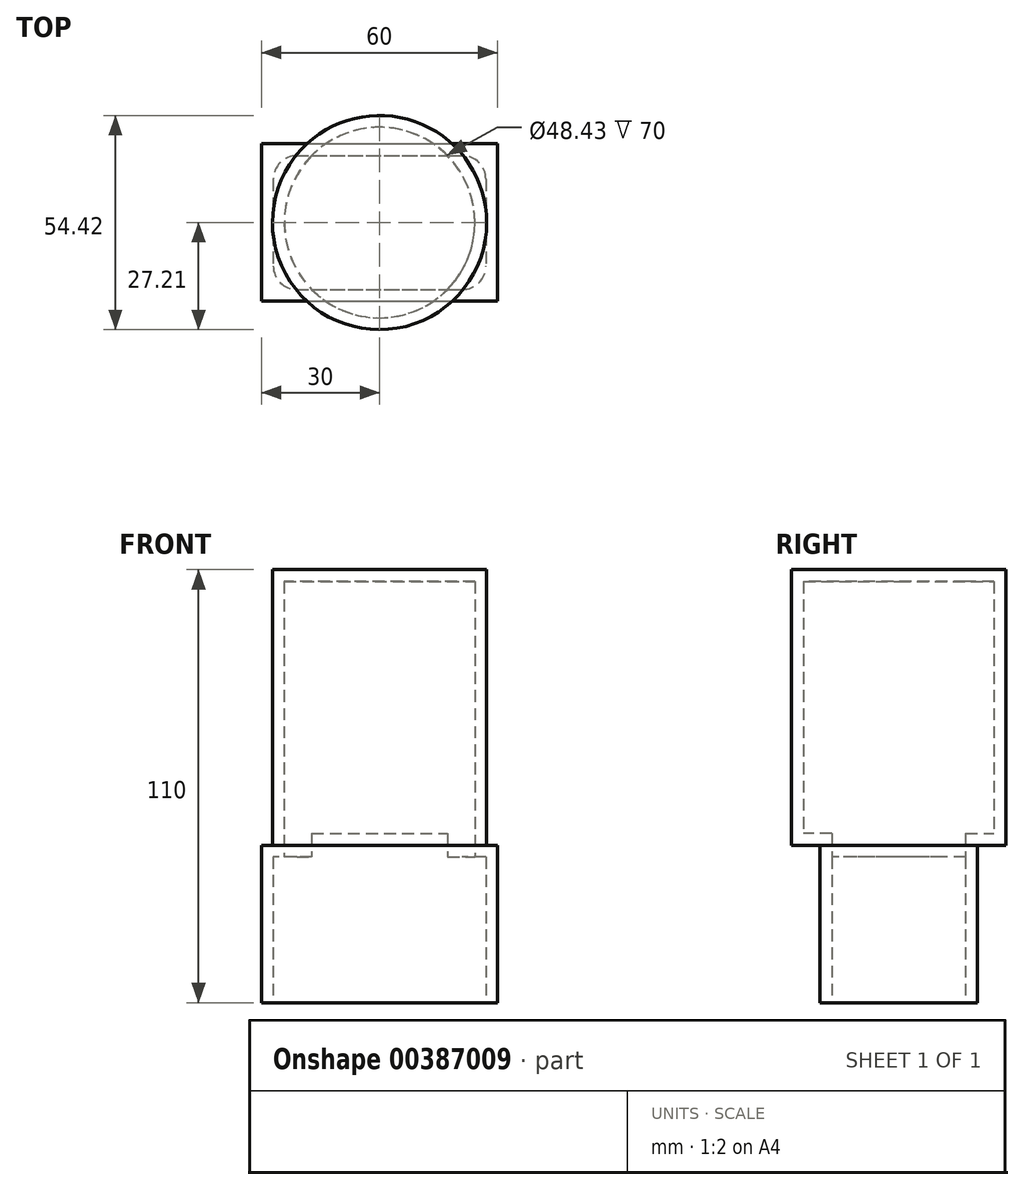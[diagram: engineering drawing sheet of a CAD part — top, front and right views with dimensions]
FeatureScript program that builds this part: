
annotation { "Feature Type Name" : "Feature", "Feature Type Description" : "" }
export const myFeature = defineFeature(function(context is Context, id is Id, definition is map)
    precondition{}
    {
        {
            var Q0;
            Q0=qCreatedBy(makeId("Top.planeOp"),FACE);
            var sketch = newSketch(context, id + "F0", { "sketchPlane" : qUnion([Q0])});
            skLineSegment(sketch, "E0.bottom", {"start": v(-30, 20) * mm, "end": v(30, 20) * mm});
            skLineSegment(sketch, "E0.top", {"start": v(-30, -20) * mm, "end": v(30, -20) * mm});
            skLineSegment(sketch, "E0.left", {"start": v(-30, 20) * mm, "end": v(-30, -20) * mm});
            skLineSegment(sketch, "E0.right", {"start": v(30, 20) * mm, "end": v(30, -20) * mm});
            skSolve(sketch);
        }
        {
            var Q0;
            Q0=makeQuery(id+"F0.imprint","IMPRINT",FACE,{"disambiguationData":[TD([[makeQuery(id+"F0.imprint","IMPRINT",EDGE,{"derivedFrom":sQuery(id+"F0.wireOp",EDGE,"E0.bottom")}),-1.0]])]});
            extrude(context, id + "F1", {"entities" : qUnion([Q0]), "depth" : 40 * mm});
        }
        {
            var Q0;
            Q0=makeQuery(id+"F1.opExtrude","CAP_FACE",FACE,{"disambiguationData":[OSD([sQuery(id+"F0.wireOp",EDGE,"E0.bottom"),sQuery(id+"F0.wireOp",EDGE,"E0.top"),sQuery(id+"F0.wireOp",EDGE,"E0.left"),sQuery(id+"F0.wireOp",EDGE,"E0.right")])],"isStart":false});
            var sketch = newSketch(context, id + "F2", { "sketchPlane" : qUnion([Q0])});
            skCircle(sketch, "E1", {"center": v(0, 0) * mm, "radius": 27.21 * mm});
            skSolve(sketch);
        }
        {
            var Q0;
            {var subQ0=sQuery(id+"F2.wireOp",EDGE,"E1");var subQ1=makeQuery(id+"F1.opExtrude","CAP_EDGE",EDGE,{"disambiguationData":[OSD([sQuery(id+"F0.wireOp",EDGE,"E0.bottom")])],"isStart":false});var subQ2=makeQuery(id+"F2.imprint","INTERSECT",VERTEX,{"disambiguationData":[OD(0.0)],"derivedFrom":[subQ1,subQ0]});Q0=makeQuery(id+"F2.imprint","IMPRINT",FACE,{"disambiguationData":[TD([[makeQuery(id+"F2.imprint","IMPRINT",EDGE,{"disambiguationData":[TD([[subQ2,-1.0]])],"derivedFrom":subQ0}),1.0]])]});}
            var Q1;
            {var subQ0=sQuery(id+"F2.wireOp",EDGE,"E1");var subQ1=makeQuery(id+"F1.opExtrude","CAP_EDGE",EDGE,{"disambiguationData":[OSD([sQuery(id+"F0.wireOp",EDGE,"E0.top")])],"isStart":false});var subQ2=makeQuery(id+"F2.imprint","INTERSECT",VERTEX,{"disambiguationData":[OD(0.0)],"derivedFrom":[subQ1,subQ0]});Q1=makeQuery(id+"F2.imprint","IMPRINT",FACE,{"disambiguationData":[TD([[makeQuery(id+"F2.imprint","IMPRINT",EDGE,{"disambiguationData":[TD([[subQ2,-1.0]])],"derivedFrom":subQ0}),1.0]])]});}
            var Q2;
            {var subQ0=sQuery(id+"F2.wireOp",EDGE,"E1");var subQ1=makeQuery(id+"F1.opExtrude","CAP_EDGE",EDGE,{"disambiguationData":[OSD([sQuery(id+"F0.wireOp",EDGE,"E0.bottom")])],"isStart":false});var subQ2=makeQuery(id+"F2.imprint","INTERSECT",VERTEX,{"disambiguationData":[OD(0.0)],"derivedFrom":[subQ1,subQ0]});Q2=makeQuery(id+"F2.imprint","IMPRINT",FACE,{"disambiguationData":[TD([[makeQuery(id+"F2.imprint","IMPRINT",EDGE,{"disambiguationData":[TD([[subQ2,1.0]])],"derivedFrom":subQ0}),1.0]])]});}
            extrude(context, id + "F3", {"entities" : qUnion([Q0, Q1, Q2]), "operationType" : NewBodyOperationType.ADD, "depth" : 70 * mm});
        }
        {
            var Q0;
            Q0=makeQuery(id+"F1.opExtrude","CAP_FACE",FACE,{"disambiguationData":[OSD([sQuery(id+"F0.wireOp",EDGE,"E0.bottom"),sQuery(id+"F0.wireOp",EDGE,"E0.top"),sQuery(id+"F0.wireOp",EDGE,"E0.left"),sQuery(id+"F0.wireOp",EDGE,"E0.right")])],"isStart":true});
            shell(context, id + "F4", {"entities" : qUnion([Q0]), "thickness" : 3 * mm});
        }
        {
            var Q0;
            Q0=makeQuery(id+"F4.opShell","OFFSET_EDGE",EDGE,{"disambiguationData":[OSD([sQuery(id+"F0.wireOp",EDGE,"E0.top"),sQuery(id+"F0.wireOp",EDGE,"E0.left")])]});
            var Q1;
            Q1=makeQuery(id+"F4.opShell","OFFSET_EDGE",EDGE,{"disambiguationData":[OSD([sQuery(id+"F0.wireOp",EDGE,"E0.bottom"),sQuery(id+"F0.wireOp",EDGE,"E0.left")])]});
            var Q2;
            Q2=makeQuery(id+"F4.opShell","OFFSET_EDGE",EDGE,{"disambiguationData":[OSD([sQuery(id+"F0.wireOp",EDGE,"E0.top"),sQuery(id+"F0.wireOp",EDGE,"E0.right")])]});
            var Q3;
            Q3=makeQuery(id+"F4.opShell","OFFSET_EDGE",EDGE,{"disambiguationData":[OSD([sQuery(id+"F0.wireOp",EDGE,"E0.bottom"),sQuery(id+"F0.wireOp",EDGE,"E0.right")])]});
            fillet(context, id + "F5", {"entities" : qUnion([Q0, Q1, Q2, Q3]), "radius" : 6 * mm, "tangentPropagation" : true, "allowEdgeOverflow" : false});
        }
    });
